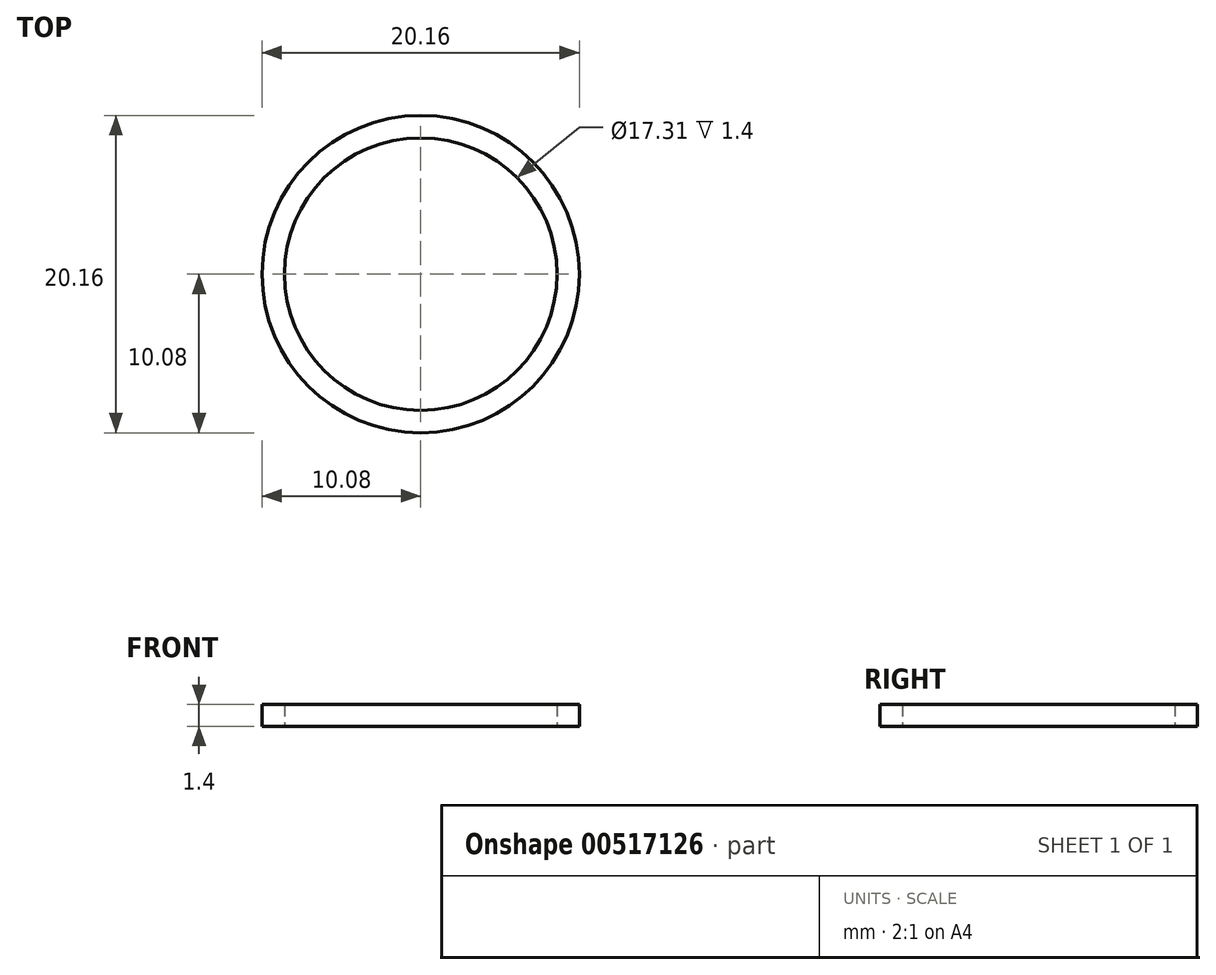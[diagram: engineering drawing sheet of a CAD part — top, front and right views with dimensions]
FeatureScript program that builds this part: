
annotation { "Feature Type Name" : "Feature", "Feature Type Description" : "" }
export const myFeature = defineFeature(function(context is Context, id is Id, definition is map)
    precondition{}
    {
        {
            var Q0;
            Q0=qCreatedBy(makeId("Top.planeOp"),FACE);
            var sketch = newSketch(context, id + "F0", { "sketchPlane" : qUnion([Q0])});
            skCircle(sketch, "E0", {"center": v(0, 0) * mm, "radius": 8.66 * mm});
            skCircle(sketch, "E1", {"center": v(0, 0) * mm, "radius": 10.08 * mm});
            skSolve(sketch);
        }
        {
            var Q0;
            Q0=makeQuery(id+"F0.imprint","IMPRINT",FACE,{"disambiguationData":[TD([[makeQuery(id+"F0.imprint","IMPRINT",EDGE,{"derivedFrom":sQuery(id+"F0.wireOp",EDGE,"E0")}),-1.0]])]});
            extrude(context, id + "F1", {"entities" : qUnion([Q0]), "depth" : 1.4 * mm, "offsetDistance" : 25 * mm});
        }
    });
